# Revit family: Drinking_Fountain-Oasis-Aqua_Pointe_Sports_Bottle_Filler-M8CRSBF
name_source: partatom
category: Plumbing Fixtures
revit_build: Autodesk Revit MEP 2013 (Build: 20130531_2115(x64)
units: mm (PartAtom-declared; Revit-internal decimal feet)

## types (2) — shared parameters
Apparent Load = 550 VA
CW Connection = No
Chiller = Yes
Cold Water Connector = Cold Water Connection
Cold Water Diameter = 0"
Cold Water Radius = 0"
Compression HP = 0 VA
Default Elevation = 2' - 3"
Description = Aqua Pointe Sports Bottle Filler
Finish = Metal - Oasis International - Brushed Stainless Steel - Exterior Finish
Full Load Amps = 5 A
Manufacturer = Oasis International
Manufacturer Fax Number = (614)322-4557
Metal Finish = Metal - Oasis International - Brushed Stainless Steel - Exterior Finish
Number of Poles = 1
Power Factor = 1
Product Name = Bi Level Radii Fountain w/ Integrated Sports Bottle Filler
Rated Watts = 550 W
Sanitary Connector = Sanitary Connection
Sanitary Diameter = 0"
Sanitary Radius = 0"
URL = http://www.oasiscoolers.com
Voltage = 115 V
Waste Connection = No
Width = 3' - 2 3/4"
zero-valued in all types: CWFU, WFU

## per-type parameters (varying)
| type | Base Rate | Product Documentation Link | Product Page URL | Rated Capacity |
| M8CRSBF | 8 GPM | http://www.oasiscoolers.com | http://www.oasiscoolers.com | 8 GPM |
| M12CRSBF | 12 GPM |  |  | 12 GPM |

note: column(s) folded — value = type name in every type: Model

## geometry (parser evidence)
native form markers: Blend x14, Sweep x25
no freeform markers — native parametric forms only
